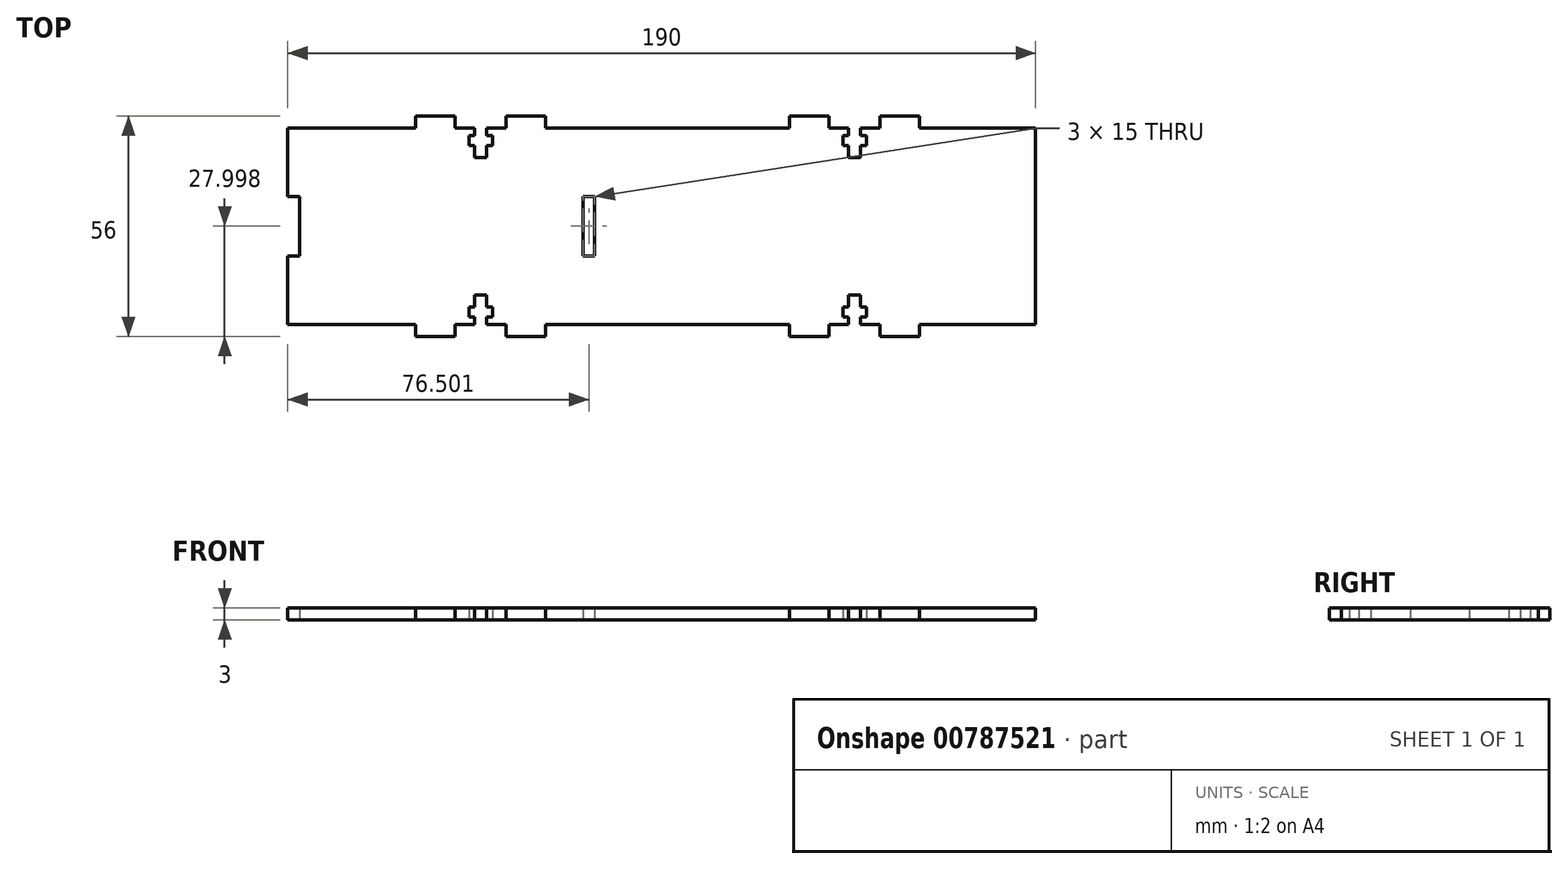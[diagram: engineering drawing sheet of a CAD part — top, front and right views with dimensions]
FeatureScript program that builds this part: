
annotation { "Feature Type Name" : "Feature", "Feature Type Description" : "" }
export const myFeature = defineFeature(function(context is Context, id is Id, definition is map)
    precondition{}
    {
        {
            var Q0;
            Q0=qCreatedBy(makeId("Top.planeOp"),FACE);
            var sketch = newSketch(context, id + "F0", { "sketchPlane" : qUnion([Q0])});
            skLineSegment(sketch, "E0.bottom", {"start": v(31.77, 0.13) * mm, "end": v(2.27, 0.13) * mm});
            skLineSegment(sketch, "E0.top", {"start": v(31.77, -49.87) * mm, "end": v(2.27, -49.87) * mm});
            skLineSegment(sketch, "E0.left", {"start": v(31.77, 0.13) * mm, "end": v(31.77, -49.87) * mm});
            skLineSegment(sketch, "E0.right", {"start": v(-158.23, 0.13) * mm, "end": v(-158.23, -17.37) * mm});
            skLineSegment(sketch, "E1", {"start": v(-109.23, 0.13) * mm, "end": v(-109.23, -49.87) * mm, "construction": true});
            skLineSegment(sketch, "E2", {"start": v(-14.23, 0.13) * mm, "end": v(-14.23, -49.87) * mm, "construction": true});
            skLineSegment(sketch, "E3", {"start": v(-12.73, 0.13) * mm, "end": v(-12.73, -1.87) * mm});
            skLineSegment(sketch, "E4", {"start": v(-12.73, -1.87) * mm, "end": v(-11.23, -1.87) * mm});
            skLineSegment(sketch, "E5", {"start": v(-11.23, -1.87) * mm, "end": v(-11.23, -4.37) * mm});
            skLineSegment(sketch, "E6", {"start": v(-11.23, -4.37) * mm, "end": v(-12.73, -4.37) * mm});
            skLineSegment(sketch, "E7", {"start": v(-12.73, -4.37) * mm, "end": v(-12.73, -7.37) * mm});
            skLineSegment(sketch, "E8", {"start": v(-12.73, -7.37) * mm, "end": v(-15.73, -7.37) * mm});
            skLineSegment(sketch, "E9", {"start": v(-15.73, -7.37) * mm, "end": v(-15.73, -4.37) * mm});
            skLineSegment(sketch, "E10", {"start": v(-15.73, -4.37) * mm, "end": v(-17.23, -4.37) * mm});
            skLineSegment(sketch, "E11", {"start": v(-17.23, -4.37) * mm, "end": v(-17.23, -1.87) * mm});
            skLineSegment(sketch, "E12", {"start": v(-17.23, -1.87) * mm, "end": v(-15.73, -1.87) * mm});
            skLineSegment(sketch, "E13", {"start": v(-15.73, -1.87) * mm, "end": v(-15.73, 0.13) * mm});
            skLineSegment(sketch, "E14.trimOffspring", {"start": v(-15.73, 0.13) * mm, "end": v(-20.73, 0.13) * mm});
            skLineSegment(sketch, "E15", {"start": v(-7.73, 0.13) * mm, "end": v(-7.73, 3.13) * mm});
            skLineSegment(sketch, "E16", {"start": v(-7.73, 3.13) * mm, "end": v(2.27, 3.13) * mm});
            skLineSegment(sketch, "E17", {"start": v(2.27, 3.13) * mm, "end": v(2.27, 0.13) * mm});
            skLineSegment(sketch, "E18.trimOffspring", {"start": v(-7.73, 0.13) * mm, "end": v(-12.73, 0.13) * mm});
            skLineSegment(sketch, "E19", {"start": v(-20.73, 0.13) * mm, "end": v(-20.73, 3.13) * mm});
            skLineSegment(sketch, "E20", {"start": v(-20.73, 3.13) * mm, "end": v(-30.73, 3.13) * mm});
            skLineSegment(sketch, "E21", {"start": v(-30.73, 3.13) * mm, "end": v(-30.73, 0.13) * mm});
            skLineSegment(sketch, "E22.trimOffspring", {"start": v(-30.73, 0.13) * mm, "end": v(-92.73, 0.13) * mm});
            skLineSegment(sketch, "E23", {"start": v(-107.73, 0.13) * mm, "end": v(-107.73, -1.87) * mm});
            skLineSegment(sketch, "E24", {"start": v(-107.73, -1.87) * mm, "end": v(-106.23, -1.87) * mm});
            skLineSegment(sketch, "E25", {"start": v(-106.23, -1.87) * mm, "end": v(-106.23, -4.37) * mm});
            skLineSegment(sketch, "E26", {"start": v(-106.23, -4.37) * mm, "end": v(-107.73, -4.37) * mm});
            skLineSegment(sketch, "E27", {"start": v(-107.73, -4.37) * mm, "end": v(-107.73, -7.37) * mm});
            skLineSegment(sketch, "E28", {"start": v(-107.73, -7.37) * mm, "end": v(-110.73, -7.37) * mm});
            skLineSegment(sketch, "E29", {"start": v(-110.73, -7.37) * mm, "end": v(-110.73, -4.37) * mm});
            skLineSegment(sketch, "E30", {"start": v(-110.73, -4.37) * mm, "end": v(-112.23, -4.37) * mm});
            skLineSegment(sketch, "E31", {"start": v(-112.23, -4.37) * mm, "end": v(-112.23, -1.87) * mm});
            skLineSegment(sketch, "E32", {"start": v(-112.23, -1.87) * mm, "end": v(-110.73, -1.87) * mm});
            skLineSegment(sketch, "E33", {"start": v(-110.73, -1.87) * mm, "end": v(-110.73, 0.13) * mm});
            skLineSegment(sketch, "E34", {"start": v(-102.73, 0.13) * mm, "end": v(-102.73, 3.13) * mm});
            skLineSegment(sketch, "E35", {"start": v(-102.73, 3.13) * mm, "end": v(-92.73, 3.13) * mm});
            skLineSegment(sketch, "E36", {"start": v(-92.73, 3.13) * mm, "end": v(-92.73, 0.13) * mm});
            skLineSegment(sketch, "E37", {"start": v(-115.73, 0.13) * mm, "end": v(-115.73, 3.13) * mm});
            skLineSegment(sketch, "E38", {"start": v(-115.73, 3.13) * mm, "end": v(-125.73, 3.13) * mm});
            skLineSegment(sketch, "E39", {"start": v(-125.73, 3.13) * mm, "end": v(-125.73, 0.13) * mm});
            skLineSegment(sketch, "E40.trimOffspring", {"start": v(-125.73, 0.13) * mm, "end": v(-158.23, 0.13) * mm});
            skLineSegment(sketch, "E41.trimOffspring", {"start": v(-110.73, 0.13) * mm, "end": v(-115.73, 0.13) * mm});
            skLineSegment(sketch, "E42", {"start": v(-107.73, 0.13) * mm, "end": v(-102.73, 0.13) * mm});
            skLineSegment(sketch, "E43", {"start": v(-110.73, -49.87) * mm, "end": v(-110.73, -47.87) * mm});
            skLineSegment(sketch, "E44", {"start": v(-110.73, -47.87) * mm, "end": v(-112.23, -47.87) * mm});
            skLineSegment(sketch, "E45", {"start": v(-112.23, -47.87) * mm, "end": v(-112.23, -45.37) * mm});
            skLineSegment(sketch, "E46", {"start": v(-112.23, -45.37) * mm, "end": v(-110.73, -45.37) * mm});
            skLineSegment(sketch, "E47", {"start": v(-110.73, -45.37) * mm, "end": v(-110.73, -42.37) * mm});
            skLineSegment(sketch, "E48", {"start": v(-110.73, -42.37) * mm, "end": v(-107.73, -42.37) * mm});
            skLineSegment(sketch, "E49", {"start": v(-107.73, -42.37) * mm, "end": v(-107.73, -45.37) * mm});
            skLineSegment(sketch, "E50", {"start": v(-107.73, -45.37) * mm, "end": v(-106.23, -45.37) * mm});
            skLineSegment(sketch, "E51", {"start": v(-106.23, -45.37) * mm, "end": v(-106.23, -47.87) * mm});
            skLineSegment(sketch, "E52", {"start": v(-106.23, -47.87) * mm, "end": v(-107.73, -47.87) * mm});
            skLineSegment(sketch, "E53", {"start": v(-107.73, -47.87) * mm, "end": v(-107.73, -49.87) * mm});
            skLineSegment(sketch, "E54", {"start": v(-115.73, -49.87) * mm, "end": v(-115.73, -52.87) * mm});
            skLineSegment(sketch, "E55", {"start": v(-115.73, -52.87) * mm, "end": v(-125.73, -52.87) * mm});
            skLineSegment(sketch, "E56", {"start": v(-125.73, -52.87) * mm, "end": v(-125.73, -49.87) * mm});
            skLineSegment(sketch, "E57", {"start": v(-102.73, -49.87) * mm, "end": v(-102.73, -52.87) * mm});
            skLineSegment(sketch, "E58", {"start": v(-102.73, -52.87) * mm, "end": v(-92.73, -52.87) * mm});
            skLineSegment(sketch, "E59", {"start": v(-92.73, -52.87) * mm, "end": v(-92.73, -49.87) * mm});
            skLineSegment(sketch, "E60.trimOffspring", {"start": v(-125.73, -49.87) * mm, "end": v(-158.23, -49.87) * mm});
            skLineSegment(sketch, "E61.trimOffspring", {"start": v(-110.73, -49.87) * mm, "end": v(-115.73, -49.87) * mm});
            skLineSegment(sketch, "E62.trimOffspring", {"start": v(-102.73, -49.87) * mm, "end": v(-107.73, -49.87) * mm});
            skLineSegment(sketch, "E63", {"start": v(-15.73, -49.87) * mm, "end": v(-15.73, -47.87) * mm});
            skLineSegment(sketch, "E64", {"start": v(-15.73, -47.87) * mm, "end": v(-17.23, -47.87) * mm});
            skLineSegment(sketch, "E65", {"start": v(-17.23, -47.87) * mm, "end": v(-17.23, -45.37) * mm});
            skLineSegment(sketch, "E66", {"start": v(-17.23, -45.37) * mm, "end": v(-15.73, -45.37) * mm});
            skLineSegment(sketch, "E67", {"start": v(-15.73, -45.37) * mm, "end": v(-15.73, -42.37) * mm});
            skLineSegment(sketch, "E68", {"start": v(-15.73, -42.37) * mm, "end": v(-12.73, -42.37) * mm});
            skLineSegment(sketch, "E69", {"start": v(-12.73, -42.37) * mm, "end": v(-12.73, -45.37) * mm});
            skLineSegment(sketch, "E70", {"start": v(-12.73, -45.37) * mm, "end": v(-11.23, -45.37) * mm});
            skLineSegment(sketch, "E71", {"start": v(-11.23, -45.37) * mm, "end": v(-11.23, -47.87) * mm});
            skLineSegment(sketch, "E72", {"start": v(-11.23, -47.87) * mm, "end": v(-12.73, -47.87) * mm});
            skLineSegment(sketch, "E73", {"start": v(-12.73, -47.87) * mm, "end": v(-12.73, -49.87) * mm});
            skLineSegment(sketch, "E74", {"start": v(-20.73, -49.87) * mm, "end": v(-20.73, -52.87) * mm});
            skLineSegment(sketch, "E75", {"start": v(-20.73, -52.87) * mm, "end": v(-30.73, -52.87) * mm});
            skLineSegment(sketch, "E76", {"start": v(-30.73, -52.87) * mm, "end": v(-30.73, -49.87) * mm});
            skLineSegment(sketch, "E77", {"start": v(-7.73, -49.87) * mm, "end": v(-7.73, -52.87) * mm});
            skLineSegment(sketch, "E78", {"start": v(-7.73, -52.87) * mm, "end": v(2.27, -52.87) * mm});
            skLineSegment(sketch, "E79", {"start": v(2.27, -52.87) * mm, "end": v(2.27, -49.87) * mm});
            skLineSegment(sketch, "E80.trimOffspring", {"start": v(-30.73, -49.87) * mm, "end": v(-92.73, -49.87) * mm});
            skLineSegment(sketch, "E81.trimOffspring", {"start": v(-15.73, -49.87) * mm, "end": v(-20.73, -49.87) * mm});
            skLineSegment(sketch, "E82.trimOffspring", {"start": v(-7.73, -49.87) * mm, "end": v(-12.73, -49.87) * mm});
            skLineSegment(sketch, "E83.bottom", {"start": v(-155.23, -17.37) * mm, "end": v(-158.23, -17.37) * mm});
            skLineSegment(sketch, "E83.top", {"start": v(-155.23, -32.37) * mm, "end": v(-158.23, -32.37) * mm});
            skLineSegment(sketch, "E83.left", {"start": v(-155.23, -17.37) * mm, "end": v(-155.23, -32.37) * mm});
            skPoint(sketch, "E83.middle", {"position": v(-158.23, -24.87) * mm});
            skLineSegment(sketch, "E84.trimOffspring", {"start": v(-158.23, -32.37) * mm, "end": v(-158.23, -49.87) * mm});
            skLineSegment(sketch, "E85.bottom", {"start": v(-83.23, -17.37) * mm, "end": v(-80.23, -17.37) * mm});
            skLineSegment(sketch, "E85.top", {"start": v(-83.23, -32.37) * mm, "end": v(-80.23, -32.37) * mm});
            skLineSegment(sketch, "E85.left", {"start": v(-83.23, -17.37) * mm, "end": v(-83.23, -32.37) * mm});
            skLineSegment(sketch, "E85.right", {"start": v(-80.23, -17.37) * mm, "end": v(-80.23, -32.37) * mm});
            skPoint(sketch, "E85.middle", {"position": v(-81.73, -24.87) * mm});
            skSolve(sketch);
        }
        {
            var Q0;
            Q0=makeQuery(id+"F0.imprint","IMPRINT",FACE,{"disambiguationData":[TD([[makeQuery(id+"F0.imprint","IMPRINT",EDGE,{"derivedFrom":sQuery(id+"F0.wireOp",EDGE,"E0.bottom")}),1.0]])]});
            extrude(context, id + "F1", {"entities" : qUnion([Q0]), "depth" : 3 * mm, "offsetDistance" : 25.4 * mm});
        }
    });
